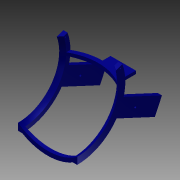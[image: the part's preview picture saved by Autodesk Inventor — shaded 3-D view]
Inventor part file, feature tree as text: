
AUTODESK INVENTOR PART (.ipt)
format: ipt  version: 2014 (Build 180170000, 170)  size: 218,624 bytes
history: native  units: in
note: dims shown in document units (in); Inventor stores cm internally (conversion verified against a paired STEP export)
features: sketch x9, revolve x3, hole x3, extrude x3, plane x2, projected_geometry x2
ambient origin geometry x8: Origin, YZ Plane, XZ Plane, XY Plane, X Axis, Y Axis, Z Axis, Center Point
bodies: Solid1 (feature_tree)
feature tree (22):
  revolve  "Revolution1"  [1 undecoded]
  revolve  "Revolution2"  [1 undecoded]
  plane  "Work Plane1"
  plane  "Work Plane2"
  revolve  "Revolution4"  [1 undecoded]
  sketch  "Sketch9"  dims[d10=12.0in d44=12.0in]
  hole  "Hole3"  [1 undecoded]
  hole  "Hole4"  [1 undecoded]
  extrude  "Extrusion3"  Depth=1.0in
  extrude  "Extrusion4"  Depth=0.72in
  hole  "Hole5"  [1 undecoded]
  extrude  "Extrusion5"  Depth=1.0in TaperAngle=0.0deg
  sketch  "Sketch14"  dims[d66=0.1718in d67=10.0in d68=0.1718in d69=1.0in d70=0.0in d71=1.0in d72=0.0in d73=6.0in d74=0.5in d75=0.75in d76=0.375in d77=0.25in d78=0.5635in d79=1.0in d80=0.8108in d81=3.5in d82=3.0in d83=0.72in d84=0.0in d85=3.0in d86=10.7316in]
  sketch  "Sketch1"  dims[d1=12.0in d3=12.0in]
  sketch  "Sketch2"  dims[d5=0.7559in d6=12.0in]
  projected_geometry  "Projected Loop1"
  sketch  "Sketch8"  dims[d7=12.0in d9=0.0275in]
  sketch  "Sketch10"  dims[d45=12.0in d46=0.0275in]
  sketch  "Sketch11"  dims[d47=0.5in]
  sketch  "Sketch12"  dims[d48=0.25in d49=0.75in d50=0.375in d51=0.25in d52=0.5635in d53=1.0in d54=0.8108in]
  sketch  "Sketch13"  dims[d55=0.25in d56=0.75in d57=0.375in d58=0.25in d59=0.5635in d60=1.0in d61=0.8108in d65=10.0in]
  projected_geometry  "Project Cut Edges2"
note: 6 required parameter values undecoded (feature->parameter linkage not recoverable at this tier; creation-order binding heuristic only, values carry confidence <= 0.55)